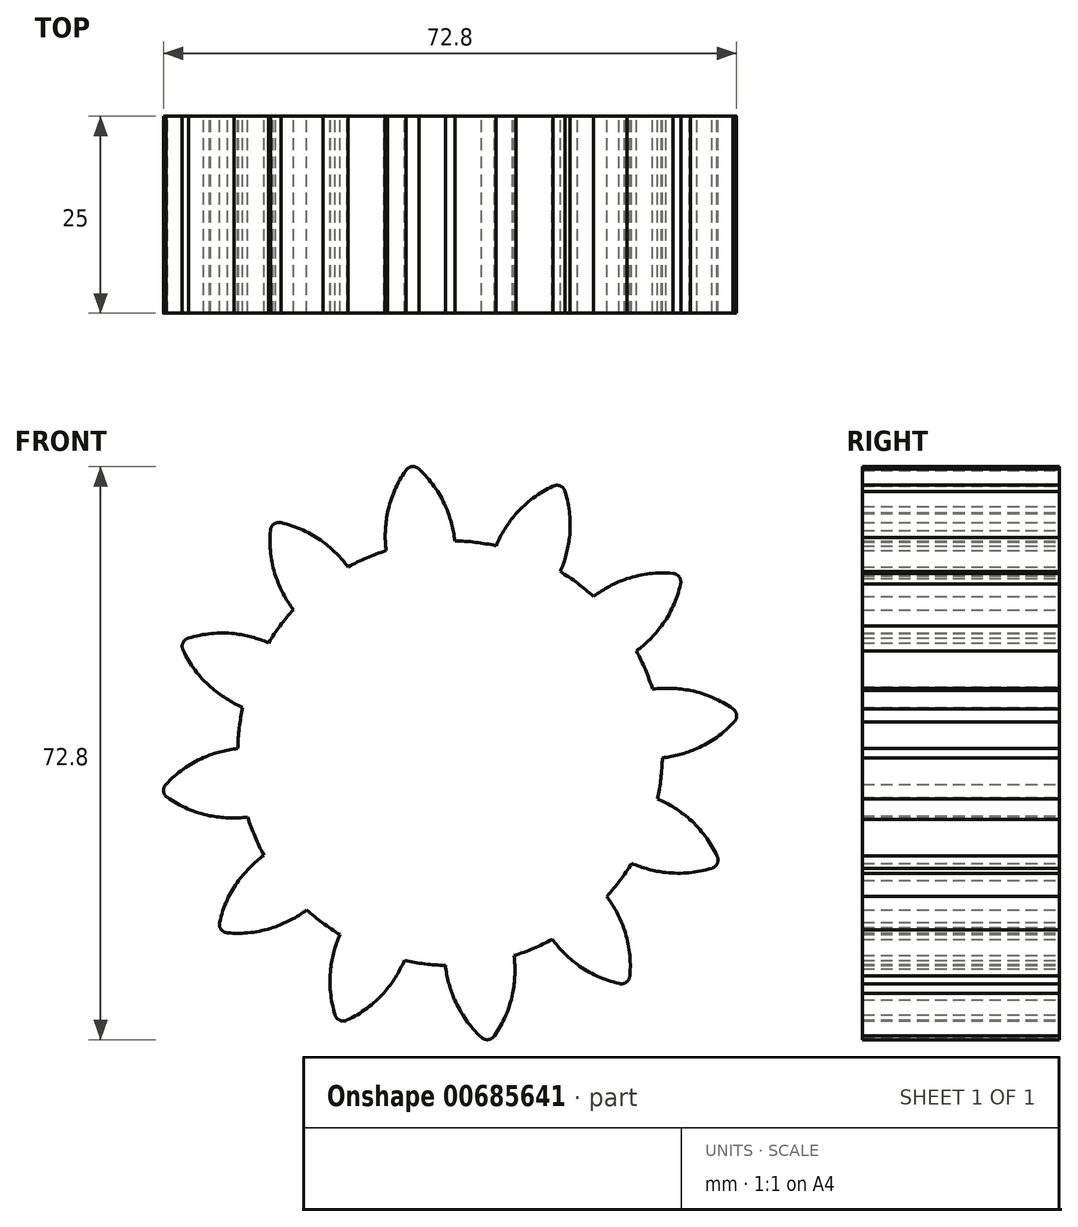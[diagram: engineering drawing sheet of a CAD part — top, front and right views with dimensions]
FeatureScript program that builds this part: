
annotation { "Feature Type Name" : "Feature", "Feature Type Description" : "" }
export const myFeature = defineFeature(function(context is Context, id is Id, definition is map)
    precondition{}
    {
        {
            var Q0;
            Q0=qCreatedBy(makeId("Front.planeOp"),FACE);
            var sketch = newSketch(context, id + "F0", { "sketchPlane" : qUnion([Q0])});
            skCircle(sketch, "E0", {"center": v(-0.45, -0.7) * mm, "radius": 58.67 * mm, "construction": true});
            skCircle(sketch, "E1", {"center": v(-0.45, -0.7) * mm, "radius": 63.5 * mm, "construction": true});
            skLineSegment(sketch, "E2", {"start": v(-0.45, -0.7) * mm, "end": v(-0.45, 115.73) * mm, "construction": true});
            skLineSegment(sketch, "E3", {"start": v(-0.45, -0.7) * mm, "end": v(-8.15, 116.67) * mm, "construction": true});
            skLineSegment(sketch, "E4", {"start": v(-0.45, 57.96) * mm, "end": v(-74.91, 57.5) * mm, "construction": true});
            skPoint(sketch, "E4.endSnap0", {"position": v(-0.45, 57.5) * mm});
            skLineSegment(sketch, "E5", {"start": v(-0.45, 57.5) * mm, "end": v(-74.35, 30.1) * mm, "construction": true});
            skCircle(sketch, "E6", {"center": v(-0.45, 57.5) * mm, "radius": 14.6 * mm, "construction": true});
            skCircle(sketch, "E7", {"center": v(-0.45, -0.7) * mm, "radius": 54.58 * mm, "construction": true});
            skCircle(sketch, "E8", {"center": v(-14.15, 52.43) * mm, "radius": 14.6 * mm, "construction": true});
            skArc(sketch, "E9", {"start": v(-0.57, 57.82) * mm, "mid": v(-0.6, 57.9) * mm, "end": v(-0.63, 57.96) * mm});
            skArc(sketch, "E10", {"start": v(-7.94, 57.48) * mm, "mid": v(-7.96, 57.4) * mm, "end": v(-7.98, 57.33) * mm});
            skCircle(sketch, "E11", {"center": v(0, 0) * mm, "radius": 26.97 * mm});
            skArc(sketch, "E12", {"start": v(-0.57, 31.33) * mm, "mid": v(-2.02, 33.88) * mm, "end": v(-3.96, 36.09) * mm});
            skArc(sketch, "E13", {"start": v(0.64, 26.56) * mm, "mid": v(0.22, 29) * mm, "end": v(-0.57, 31.33) * mm});
            skArc(sketch, "E14.MirrorCS", {"start": v(-7.95, 30.55) * mm, "mid": v(-7.06, 33.35) * mm, "end": v(-5.63, 35.91) * mm});
            skArc(sketch, "E15.MirrorCS", {"start": v(-8.13, 25.72) * mm, "mid": v(-8.23, 28.14) * mm, "end": v(-7.95, 30.55) * mm});
            skArc(sketch, "E16", {"start": v(-3.96, 36.09) * mm, "mid": v(-4.84, 36.4) * mm, "end": v(-5.63, 35.91) * mm});
            skSolve(sketch);
        }
        {
            var Q0;
            {var subQ1=sQuery(id+"F0.wireOp",EDGE,"E12");Q0=makeQuery(id+"F0.imprint","IMPRINT",FACE,{"disambiguationData":[TD([[makeQuery(id+"F0.imprint","IMPRINT",EDGE,{"derivedFrom":subQ1}),1.0]])]});}
            var Q1;
            {var subQ0=sQuery(id+"F0.wireOp",EDGE,"E11");var subQ1=makeQuery(id+"F0.imprint","INTERSECT",VERTEX,{"derivedFrom":[subQ0,sQuery(id+"F0.wireOp",EDGE,"E15.MirrorCS")]});Q1=makeQuery(id+"F0.imprint","IMPRINT",FACE,{"disambiguationData":[TD([[makeQuery(id+"F0.imprint","IMPRINT",EDGE,{"disambiguationData":[TD([[subQ1,1.0]])],"derivedFrom":subQ0}),1.0]])]});}
            extrude(context, id + "F1", {"entities" : qUnion([Q0, Q1]), "depth" : 25 * mm, "offsetDistance" : 25 * mm});
        }
        {
            var Q0;
            Q0=makeQuery(id+"F1.opExtrude","SWEPT_BODY",BODY,{"disambiguationData":[OSD([sQuery(id+"F0.wireOp",EDGE,"E11"),sQuery(id+"F0.wireOp",EDGE,"E12"),sQuery(id+"F0.wireOp",EDGE,"E13"),sQuery(id+"F0.wireOp",EDGE,"E14.MirrorCS"),sQuery(id+"F0.wireOp",EDGE,"E15.MirrorCS"),sQuery(id+"F0.wireOp",EDGE,"E16")])]});
            var Q1;
            Q1=makeQuery(id+"F1.opExtrude","SWEPT_FACE",FACE,{"disambiguationData":[OSD([sQuery(id+"F0.wireOp",EDGE,"E11")])]});
            circularPattern(context, id + "F2", {"operationType" : NewBodyOperationType.ADD, "entities" : qUnion([Q0]), "axis" : qUnion([Q1]), "angle" : 360 * degree, "instanceCount" : 12, "equalSpace" : true});
        }
    });
